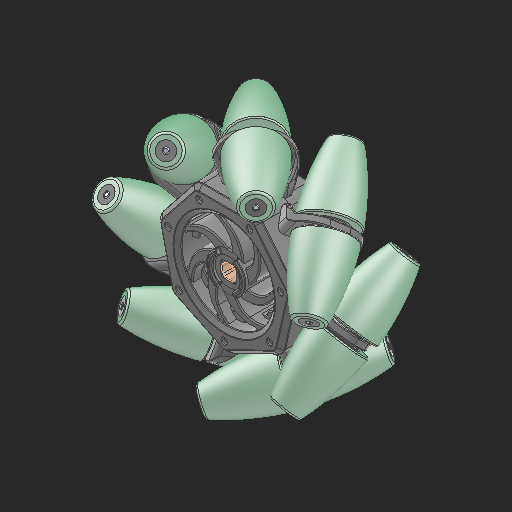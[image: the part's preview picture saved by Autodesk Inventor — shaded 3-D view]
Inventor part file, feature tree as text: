
AUTODESK INVENTOR PART (.ipt)
format: ipt  version: 2023 (Build 270158000, 158)  size: 18,179,072 bytes
history: native  units: in
note: dims shown in document units (in); Inventor stores cm internally (conversion verified against a paired STEP export)
features: other x46, move_body x1, sketch x1, extrude x1
ambient origin geometry x8: Origin, YZ Plane, XZ Plane, XY Plane, X Axis, Y Axis, Z Axis, Center Point
bodies: Solid1 (feature_tree), Solid2 (feature_tree), Solid3 (feature_tree), Solid4 (feature_tree), Solid5 (feature_tree), Solid6 (feature_tree), Solid7 (feature_tree), Solid8 (feature_tree), Solid9 (feature_tree), Solid10 (feature_tree), Solid11 (feature_tree), Solid12 (feature_tree), Solid13 (feature_tree), Solid14 (feature_tree), Solid15 (feature_tree), Solid16 (feature_tree), Solid17 (feature_tree), Solid18 (feature_tree), Solid19 (feature_tree), Solid20 (feature_tree), Solid21 (feature_tree), Solid22 (feature_tree), Solid23 (feature_tree), Solid24 (feature_tree), Solid25 (feature_tree), Solid26 (feature_tree), Solid27 (feature_tree), Solid28 (feature_tree), Solid29 (feature_tree), Solid30 (feature_tree), Solid31 (feature_tree), Solid32 (feature_tree), Solid33 (feature_tree), Solid34 (feature_tree), Solid35 (feature_tree), Solid36 (feature_tree), Solid37 (feature_tree), Solid38 (feature_tree), Solid39 (feature_tree), Solid40 (feature_tree), Solid41 (feature_tree), Solid42 (feature_tree), Solid43 (feature_tree), Solid44 (feature_tree)
feature tree (49):
  other  "4 Mecanum Wheel (276-1447) .iam"
  other  "276-1447-002 Rev3.ipt:1"
  other  "276-1447-001 Rev3.ipt:1"
  other  "276-1447-010 Rev1.iam:1::276-1447-011 Rev1.ipt:1"
  other  "276-1447-010 Rev1.iam:1::276-1447-012 Rev1.ipt:1"
  other  "276-1447-010 Rev1.iam:1::276-1447-013 Rev1.ipt:1"
  other  "276-1447-010 Rev1.iam:1::276-1447-015 Rev1.ipt:1"
  other  "276-1447-010 Rev1.iam:1::276-1447-015 Rev1.ipt:2"
  other  "276-1447-010 Rev1.iam:1::276-1447-012 Rev1.ipt:2"
  other  "276-1447-010 Rev1.iam:2::276-1447-011 Rev1.ipt:1"
  other  "276-1447-010 Rev1.iam:2::276-1447-012 Rev1.ipt:1"
  other  "276-1447-010 Rev1.iam:2::276-1447-013 Rev1.ipt:1"
  other  "276-1447-010 Rev1.iam:2::276-1447-015 Rev1.ipt:1"
  other  "276-1447-010 Rev1.iam:2::276-1447-015 Rev1.ipt:2"
  other  "276-1447-010 Rev1.iam:2::276-1447-012 Rev1.ipt:2"
  other  "276-1447-010 Rev1.iam:3::276-1447-011 Rev1.ipt:1"
  other  "276-1447-010 Rev1.iam:3::276-1447-012 Rev1.ipt:1"
  other  "276-1447-010 Rev1.iam:3::276-1447-013 Rev1.ipt:1"
  other  "276-1447-010 Rev1.iam:3::276-1447-015 Rev1.ipt:1"
  other  "276-1447-010 Rev1.iam:3::276-1447-015 Rev1.ipt:2"
  other  "276-1447-010 Rev1.iam:3::276-1447-012 Rev1.ipt:2"
  other  "276-1447-010 Rev1.iam:4::276-1447-011 Rev1.ipt:1"
  other  "276-1447-010 Rev1.iam:4::276-1447-012 Rev1.ipt:1"
  other  "276-1447-010 Rev1.iam:4::276-1447-013 Rev1.ipt:1"
  other  "276-1447-010 Rev1.iam:4::276-1447-015 Rev1.ipt:1"
  other  "276-1447-010 Rev1.iam:4::276-1447-015 Rev1.ipt:2"
  other  "276-1447-010 Rev1.iam:4::276-1447-012 Rev1.ipt:2"
  other  "276-1447-010 Rev1.iam:5::276-1447-011 Rev1.ipt:1"
  other  "276-1447-010 Rev1.iam:5::276-1447-012 Rev1.ipt:1"
  other  "276-1447-010 Rev1.iam:5::276-1447-013 Rev1.ipt:1"
  other  "276-1447-010 Rev1.iam:5::276-1447-015 Rev1.ipt:1"
  other  "276-1447-010 Rev1.iam:5::276-1447-015 Rev1.ipt:2"
  other  "276-1447-010 Rev1.iam:5::276-1447-012 Rev1.ipt:2"
  other  "276-1447-010 Rev1.iam:6::276-1447-011 Rev1.ipt:1"
  other  "276-1447-010 Rev1.iam:6::276-1447-012 Rev1.ipt:1"
  other  "276-1447-010 Rev1.iam:6::276-1447-013 Rev1.ipt:1"
  other  "276-1447-010 Rev1.iam:6::276-1447-015 Rev1.ipt:1"
  other  "276-1447-010 Rev1.iam:6::276-1447-015 Rev1.ipt:2"
  other  "276-1447-010 Rev1.iam:6::276-1447-012 Rev1.ipt:2"
  other  "276-1447-010 Rev1.iam:7::276-1447-011 Rev1.ipt:1"
  other  "276-1447-010 Rev1.iam:7::276-1447-012 Rev1.ipt:1"
  other  "276-1447-010 Rev1.iam:7::276-1447-013 Rev1.ipt:1"
  other  "276-1447-010 Rev1.iam:7::276-1447-015 Rev1.ipt:1"
  other  "276-1447-010 Rev1.iam:7::276-1447-015 Rev1.ipt:2"
  other  "276-1447-010 Rev1.iam:7::276-1447-012 Rev1.ipt:2"
  move_body  "Move Body1"
  sketch  "Sketch1"  dims[d0=0.3937in d1=1.0in d2=0.0in d3=90.0deg d4=0.0344in]
  other  "Srf1"
  extrude  "ExtrusionSrf1"  Depth=0.3937in TaperAngle=0.0deg
